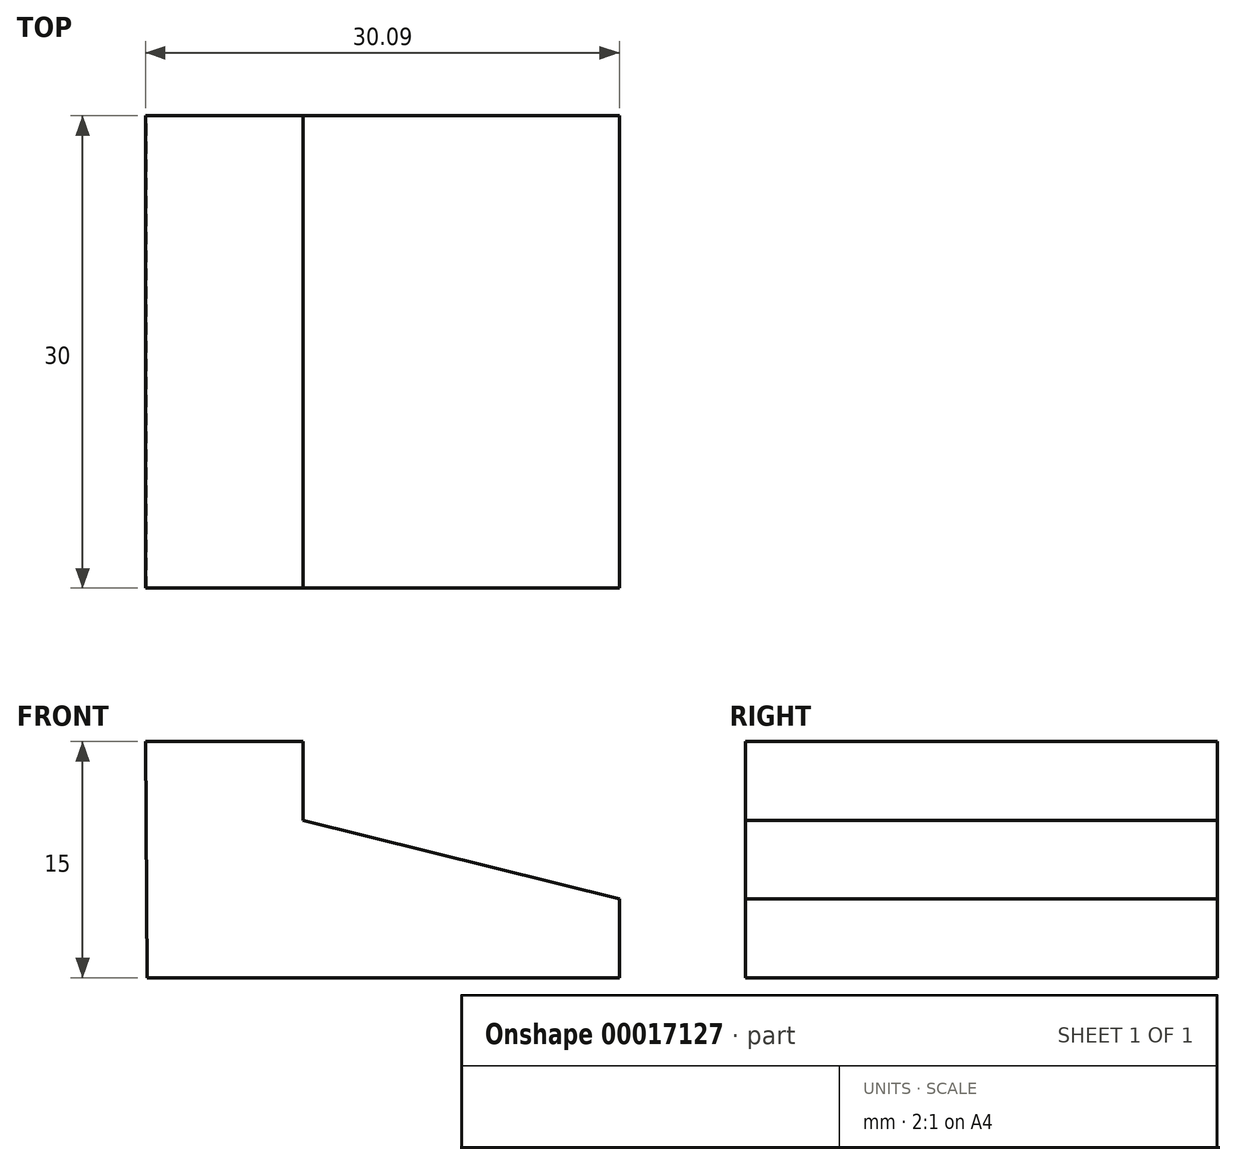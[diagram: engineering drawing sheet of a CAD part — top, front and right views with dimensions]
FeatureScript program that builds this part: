
annotation { "Feature Type Name" : "Feature", "Feature Type Description" : "" }
export const myFeature = defineFeature(function(context is Context, id is Id, definition is map)
    precondition{}
    {
        {
            var Q0;
            Q0=qCreatedBy(makeId("Front.planeOp"),FACE);
            var sketch = newSketch(context, id + "F0", { "sketchPlane" : qUnion([Q0])});
            skLineSegment(sketch, "E0", {"start": v(-14.34, 3.79) * mm, "end": v(15.66, 3.79) * mm});
            skLineSegment(sketch, "E1", {"start": v(15.66, 3.79) * mm, "end": v(15.66, 8.79) * mm});
            skLineSegment(sketch, "E2", {"start": v(15.66, 8.79) * mm, "end": v(-4.43, 13.79) * mm});
            skLineSegment(sketch, "E3", {"start": v(-4.43, 13.79) * mm, "end": v(-4.43, 18.79) * mm});
            skLineSegment(sketch, "E4", {"start": v(-14.43, 18.79) * mm, "end": v(-4.43, 18.79) * mm});
            skLineSegment(sketch, "E5", {"start": v(-14.34, 3.79) * mm, "end": v(-14.43, 18.79) * mm});
            skSolve(sketch);
        }
        {
            var Q0;
            Q0=makeQuery(id+"F0.imprint","IMPRINT",FACE,{"disambiguationData":[TD([[makeQuery(id+"F0.imprint","IMPRINT",EDGE,{"derivedFrom":sQuery(id+"F0.wireOp",EDGE,"E0")}),1.0]])]});
            extrude(context, id + "F1", {"entities" : qUnion([Q0]), "depth" : 30 * mm});
        }
    });
